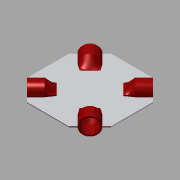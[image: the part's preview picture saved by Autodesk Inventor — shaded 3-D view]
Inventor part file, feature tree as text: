
AUTODESK INVENTOR PART (.ipt)
format: ipt  version: 2015 (Build 190159000, 159)  size: 587,264 bytes
history: native  units: in
note: dims shown in document units (in); Inventor stores cm internally (conversion verified against a paired STEP export)
features: sketch x5, extrude x4, plane x3, other x3, loft x2, pattern_circular x2
ambient origin geometry x8: Origin, YZ Plane, XZ Plane, XY Plane, X Axis, Y Axis, Z Axis, Center Point
bodies: Solid1 (feature_tree)
feature tree (19):
  extrude  "Extrusion1"  TaperAngle=0.0deg  [1 undecoded]
  plane  "Work Plane1"
  extrude  "Extrusion4"  Depth=1.1811in TaperAngle=0.0deg
  extrude  "Extrusion5"  TaperAngle=0.0deg  [1 undecoded]
  loft  "Loft1"
  plane  "Work Plane3"
  pattern_circular  "Circular Pattern1"  Count=4 Angle=360.0deg
  plane  "Work Plane5"
  loft  "Loft5"
  extrude  "Extrusion8"  Depth=0.7874in
  pattern_circular  "Circular Pattern3"  [2 undecoded]
  sketch  "Sketch3"  dims[d11=0.0787in d12=0.0in d16=0.0in]
  sketch  "Sketch7"  dims[d25=1.2205in d26=1.1811in d27=0.0in]
  sketch  "Sketch8"  dims[d29=1.9685in d30=0.0in d34=0.0in d35=90.0deg]
  other  "Edges1"
  other  "Edges2"
  sketch  "Sketch15"  dims[d36=0.0in d37=90.0deg d38=0.7874in d52=1.5748in d53=360.0deg]
  other  "Edges7"
  sketch  "Sketch16"  dims[d58=1.378in d59=1.6535in d76=0.7874in d77=1.378in d78=0.0in d79=90.0deg d80=0.0in d81=90.0deg d82=0.1969in d83=0.0in d84=1.5748in d85=360.0deg]
note: 4 required parameter values undecoded (feature->parameter linkage not recoverable at this tier; creation-order binding heuristic only, values carry confidence <= 0.55)
